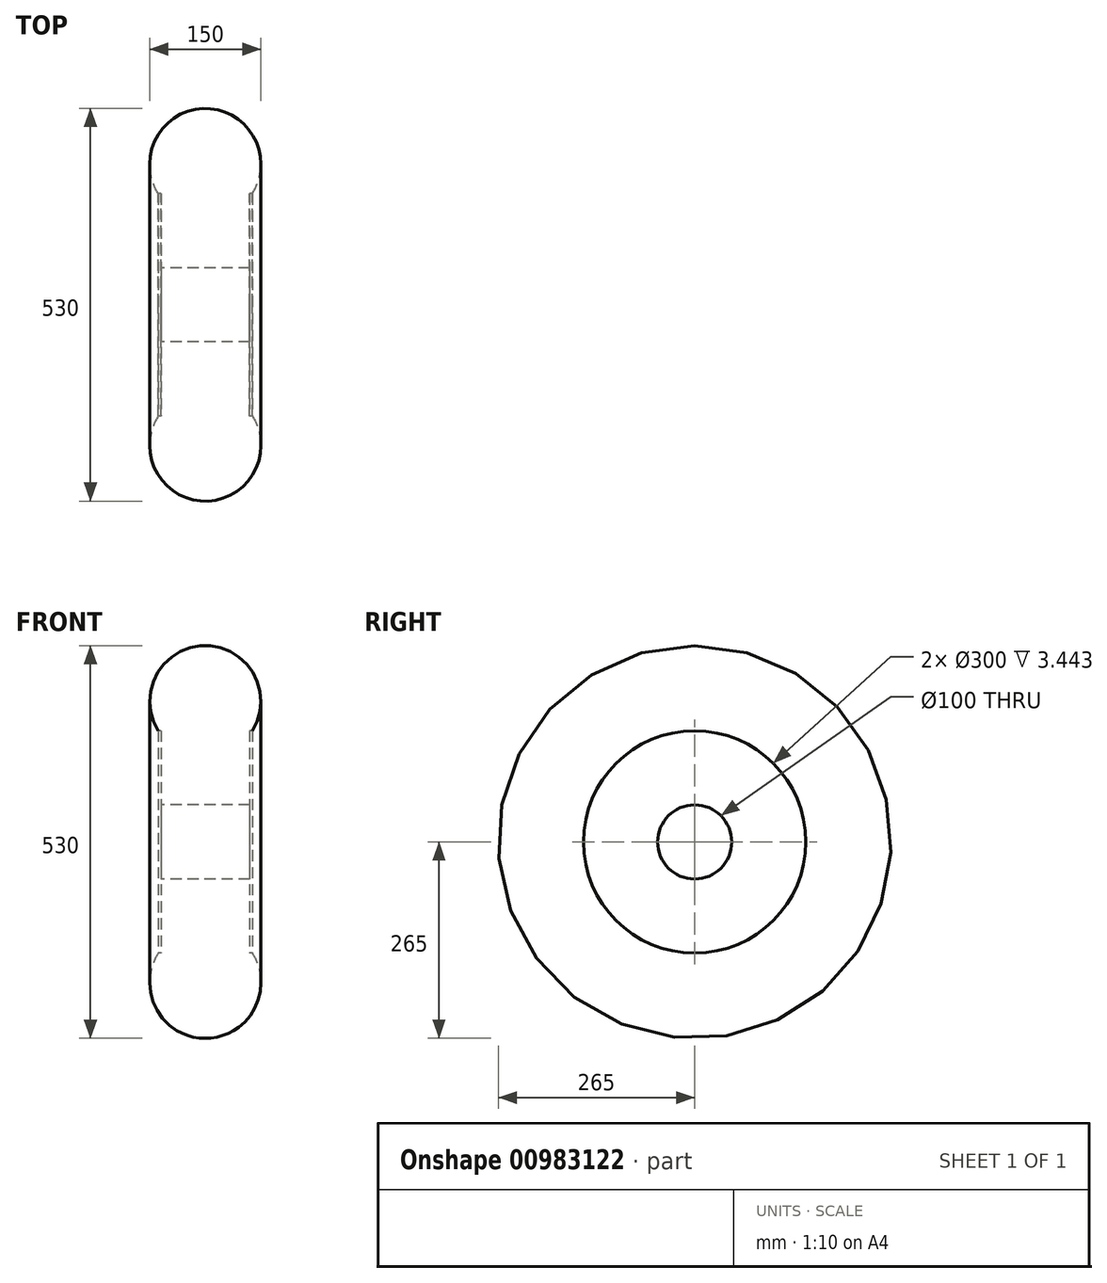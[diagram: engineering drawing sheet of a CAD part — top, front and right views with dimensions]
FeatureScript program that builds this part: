
annotation { "Feature Type Name" : "Feature", "Feature Type Description" : "" }
export const myFeature = defineFeature(function(context is Context, id is Id, definition is map)
    precondition{}
    {
        {
            var Q0;
            Q0=qCreatedBy(makeId("Top.planeOp"),FACE);
            var sketch = newSketch(context, id + "F0", { "sketchPlane" : qUnion([Q0])});
            skArc(sketch, "E0", {"start": v(63.44, -40) * mm, "mid": v(0, 75) * mm, "end": v(-63.44, -40) * mm});
            skLineSegment(sketch, "E1", {"start": v(0, -140) * mm, "end": v(0, -190) * mm});
            skLineSegment(sketch, "E2", {"start": v(-79.46, -190) * mm, "end": v(95.04, -190) * mm, "construction": true});
            skLineSegment(sketch, "E3", {"start": v(-63.44, -40) * mm, "end": v(-60, -40) * mm});
            skLineSegment(sketch, "E4", {"start": v(-60, -40) * mm, "end": v(-60, -140) * mm});
            skLineSegment(sketch, "E5", {"start": v(-60, -140) * mm, "end": v(0, -140) * mm});
            skLineSegment(sketch, "E6.trimOffspring", {"start": v(60, -40) * mm, "end": v(63.44, -40) * mm});
            skLineSegment(sketch, "E7.MirrorCS", {"start": v(60, -140) * mm, "end": v(0, -140) * mm});
            skLineSegment(sketch, "E8.MirrorCS", {"start": v(60, -40) * mm, "end": v(60, -140) * mm});
            skLineSegment(sketch, "E9.MirrorCS", {"start": v(63.44, -40) * mm, "end": v(60, -40) * mm});
            skSolve(sketch);
        }
        {
            var Q0;
            Q0 = qSketchRegion(id + "F0", true);
            var Q1;
            Q1=sQuery(id+"F0.wireOp",EDGE,"E2");
            revolve(context, id + "F1", {"surfaceOperationType" : NewSurfaceOperationType.NEW, "entities" : qUnion([Q0]), "axis" : qUnion([Q1]), "revolveType" : RevolveType.FULL});
        }
    });
